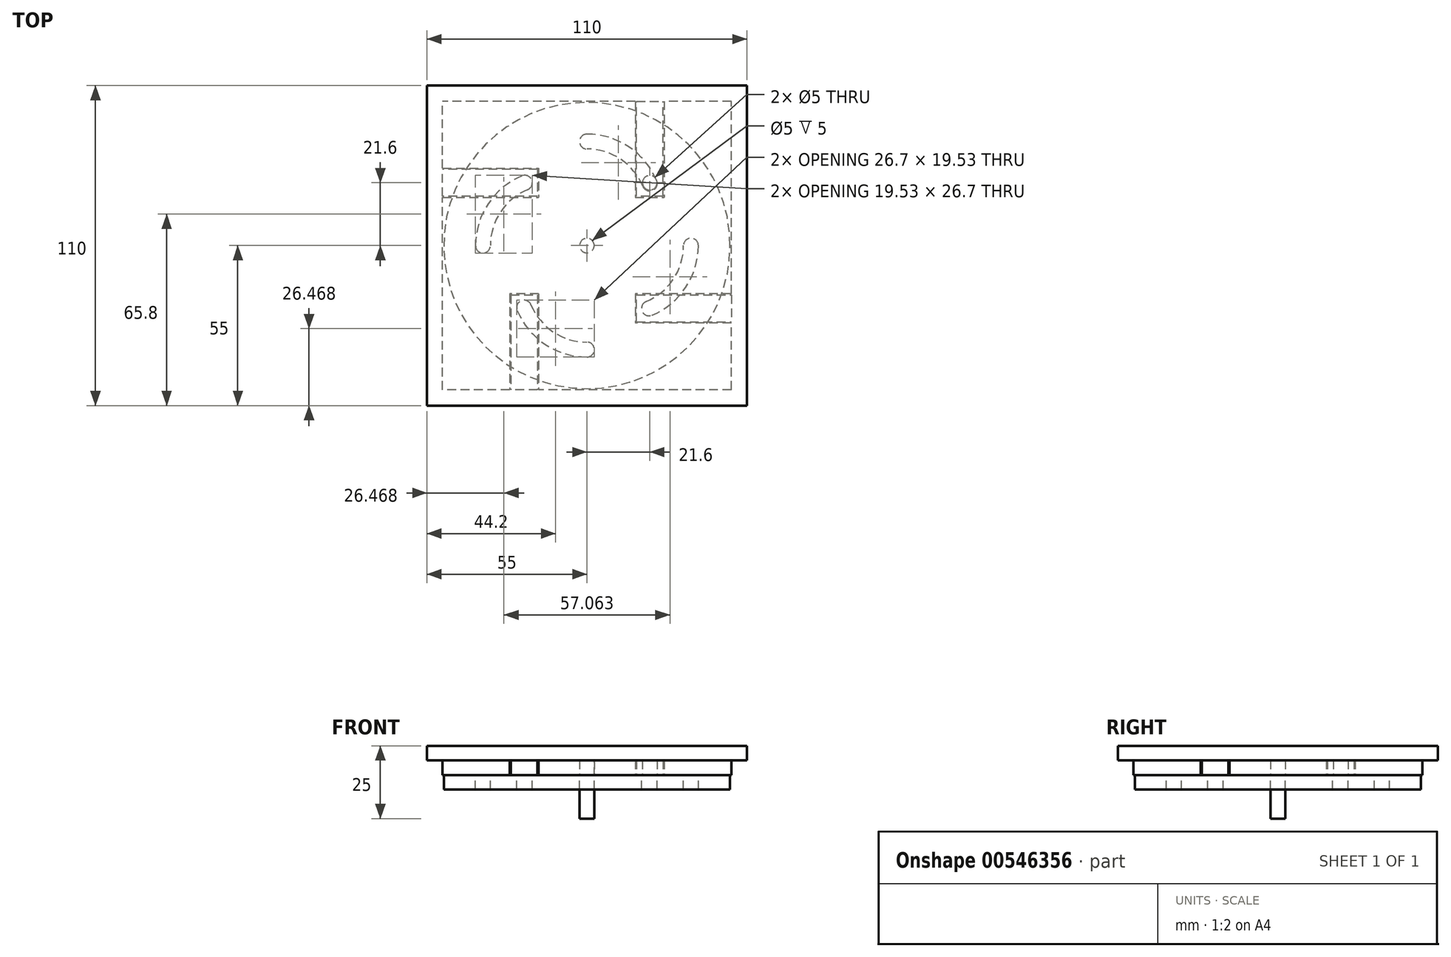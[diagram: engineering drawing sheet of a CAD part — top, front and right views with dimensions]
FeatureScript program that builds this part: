
annotation { "Feature Type Name" : "Feature", "Feature Type Description" : "" }
export const myFeature = defineFeature(function(context is Context, id is Id, definition is map)
    precondition{}
    {
        {
            assignVariable(context, id + "F0", {"name" : "thickness", "anyValue" : 5});
        }
        {
            assignVariable(context, id + "F1", {"name" : "boltsize", "anyValue" : 5});
        }
        {
            var Q0;
            Q0=qCreatedBy(makeId("Top.planeOp"),FACE);
            var sketch = newSketch(context, id + "F2", { "sketchPlane" : qUnion([Q0])});
            skPoint(sketch, "E0.middle", {"position": v(0, 0) * mm});
            skLineSegment(sketch, "E1.bottom", {"start": v(-49.6, 26.6) * mm, "end": v(-16.6, 26.6) * mm});
            skLineSegment(sketch, "E1.top", {"start": v(-49.6, 16.6) * mm, "end": v(-16.6, 16.6) * mm});
            skLineSegment(sketch, "E1.left", {"start": v(-49.6, 26.6) * mm, "end": v(-49.6, 16.6) * mm});
            skLineSegment(sketch, "E2.bottom", {"start": v(16.6, 49.6) * mm, "end": v(26.6, 49.6) * mm});
            skLineSegment(sketch, "E2.top", {"start": v(16.6, 16.6) * mm, "end": v(26.6, 16.6) * mm});
            skLineSegment(sketch, "E2.left", {"start": v(16.6, 49.6) * mm, "end": v(16.6, 16.6) * mm});
            skLineSegment(sketch, "E2.right", {"start": v(26.6, 49.6) * mm, "end": v(26.6, 16.6) * mm});
            skLineSegment(sketch, "E3.bottom", {"start": v(49.6, -16.6) * mm, "end": v(16.6, -16.6) * mm});
            skLineSegment(sketch, "E3.top", {"start": v(49.6, -26.6) * mm, "end": v(16.6, -26.6) * mm});
            skLineSegment(sketch, "E3.left", {"start": v(49.6, -16.6) * mm, "end": v(49.6, -26.6) * mm});
            skLineSegment(sketch, "E3.right", {"start": v(16.6, -16.6) * mm, "end": v(16.6, -26.6) * mm});
            skLineSegment(sketch, "E4.bottom", {"start": v(-16.6, -16.6) * mm, "end": v(-26.6, -16.6) * mm});
            skLineSegment(sketch, "E4.top", {"start": v(-16.6, -49.6) * mm, "end": v(-26.6, -49.6) * mm});
            skLineSegment(sketch, "E4.left", {"start": v(-16.6, -16.6) * mm, "end": v(-16.6, -49.6) * mm});
            skLineSegment(sketch, "E4.right", {"start": v(-26.6, -16.6) * mm, "end": v(-26.6, -49.6) * mm});
            skLineSegment(sketch, "E5.bottom", {"start": v(49.6, -49.6) * mm, "end": v(-49.6, -49.6) * mm});
            skLineSegment(sketch, "E5.top", {"start": v(49.6, 49.6) * mm, "end": v(-49.6, 49.6) * mm});
            skLineSegment(sketch, "E5.left", {"start": v(49.6, -49.6) * mm, "end": v(49.6, 49.6) * mm});
            skLineSegment(sketch, "E5.right", {"start": v(-49.6, -49.6) * mm, "end": v(-49.6, 49.6) * mm});
            skLineSegment(sketch, "E6", {"start": v(-16.6, 26.6) * mm, "end": v(-16.6, 16.6) * mm});
            skLineSegment(sketch, "E7.bottom", {"start": v(16.6, 16.6) * mm, "end": v(-16.6, 16.6) * mm, "construction": true});
            skLineSegment(sketch, "E7.top", {"start": v(16.6, -16.6) * mm, "end": v(-16.6, -16.6) * mm, "construction": true});
            skLineSegment(sketch, "E7.left", {"start": v(16.6, 16.6) * mm, "end": v(16.6, -16.6) * mm, "construction": true});
            skLineSegment(sketch, "E7.right", {"start": v(-16.6, 16.6) * mm, "end": v(-16.6, -16.6) * mm, "construction": true});
            skLineSegment(sketch, "E8.bottom", {"start": v(50, 50) * mm, "end": v(-50, 50) * mm, "construction": true});
            skLineSegment(sketch, "E8.top", {"start": v(50, -50) * mm, "end": v(-50, -50) * mm, "construction": true});
            skLineSegment(sketch, "E8.left", {"start": v(50, 50) * mm, "end": v(50, -50) * mm, "construction": true});
            skLineSegment(sketch, "E8.right", {"start": v(-50, 50) * mm, "end": v(-50, -50) * mm, "construction": true});
            skLineSegment(sketch, "E9.bottom", {"start": v(21.6, 21.6) * mm, "end": v(-21.6, 21.6) * mm, "construction": true});
            skLineSegment(sketch, "E9.top", {"start": v(21.6, -21.6) * mm, "end": v(-21.6, -21.6) * mm, "construction": true});
            skLineSegment(sketch, "E9.left", {"start": v(21.6, 21.6) * mm, "end": v(21.6, -21.6) * mm, "construction": true});
            skLineSegment(sketch, "E9.right", {"start": v(-21.6, 21.6) * mm, "end": v(-21.6, -21.6) * mm, "construction": true});
            skPoint(sketch, "E9.cornerSnap0", {"position": v(21.6, 16.6) * mm});
            skPoint(sketch, "E10", {"position": v(-16.6, 21.6) * mm});
            skLineSegment(sketch, "E11.bottom", {"start": v(26.2, 17) * mm, "end": v(17, 17) * mm});
            skLineSegment(sketch, "E11.top", {"start": v(26.2, 49.6) * mm, "end": v(17, 49.6) * mm});
            skLineSegment(sketch, "E11.left", {"start": v(26.2, 17) * mm, "end": v(26.2, 49.6) * mm});
            skLineSegment(sketch, "E11.right", {"start": v(17, 17) * mm, "end": v(17, 49.6) * mm});
            skPoint(sketch, "E11.middle", {"position": v(21.6, 33.3) * mm});
            skPoint(sketch, "E12", {"position": v(21.6, 17) * mm});
            skCircle(sketch, "E13", {"center": v(0, 0) * mm, "radius": 2.5 * mm});
            skSolve(sketch);
        }
        {
            var Q0;
            Q0=qCreatedBy(makeId("Top.planeOp"),FACE);
            var sketch = newSketch(context, id + "F3", { "sketchPlane" : qUnion([Q0])});
            skLineSegment(sketch, "E14.0", {"start": v(50, 50) * mm, "end": v(-50, 50) * mm});
            skLineSegment(sketch, "E15.0", {"start": v(-50, 50) * mm, "end": v(-50, -50) * mm});
            skLineSegment(sketch, "E16.0", {"start": v(50, 50) * mm, "end": v(50, -50) * mm});
            skLineSegment(sketch, "E17.0", {"start": v(50, -50) * mm, "end": v(-50, -50) * mm});
            skLineSegment(sketch, "E18.0", {"start": v(55, 55) * mm, "end": v(-55, 55) * mm});
            skLineSegment(sketch, "E18.1", {"start": v(55, 55) * mm, "end": v(55, -55) * mm});
            skLineSegment(sketch, "E18.2", {"start": v(55, -55) * mm, "end": v(-55, -55) * mm});
            skLineSegment(sketch, "E18.3", {"start": v(-55, 55) * mm, "end": v(-55, -55) * mm});
            skSolve(sketch);
        }
        {
            var Q0;
            {var subQ4=sQuery(id+"F2.wireOp",EDGE,"E1.bottom");Q0=makeQuery(id+"F2.imprint","IMPRINT",FACE,{"disambiguationData":[TD([[makeQuery(id+"F2.imprint","IMPRINT",EDGE,{"derivedFrom":subQ4}),1.0]])]});}
            extrude(context, id + "F4", {"entities" : qUnion([Q0]), "depth" : (getVariable(context, 'thickness')) * mm, "offsetDistance" : 25 * mm});
        }
        {
            var Q0;
            Q0=makeQuery(id+"F3.imprint","IMPRINT",FACE,{"disambiguationData":[TD([[makeQuery(id+"F3.imprint","IMPRINT",EDGE,{"derivedFrom":sQuery(id+"F3.wireOp",EDGE,"E14.0")}),-1.0]])]});
            var Q1;
            Q1=makeQuery(id+"F3.imprint","IMPRINT",FACE,{"disambiguationData":[TD([[makeQuery(id+"F3.imprint","IMPRINT",EDGE,{"derivedFrom":sQuery(id+"F3.wireOp",EDGE,"E14.0")}),1.0]])]});
            extrude(context, id + "F5", {"entities" : qUnion([Q0, Q1]), "operationType" : NewBodyOperationType.ADD, "depth" : 10 * mm, "offsetDistance" : 25 * mm, "hasSecondDirection" : true, "secondDirectionOppositeDirection" : false, "secondDirectionDepth" : 5 * mm});
        }
        {
            var Q0;
            Q0=makeQuery(id+"F2.imprint","IMPRINT",FACE,{"disambiguationData":[TD([[makeQuery(id+"F2.imprint","IMPRINT",EDGE,{"derivedFrom":sQuery(id+"F2.wireOp",EDGE,"E11.bottom")}),-1.0]])]});
            extrude(context, id + "F6", {"entities" : qUnion([Q0]), "depth" : (getVariable(context, 'thickness')) * mm, "offsetDistance" : 25 * mm});
        }
        {
            var Q0;
            Q0=qCreatedBy(makeId("Front.planeOp"),FACE);
            var sketch = newSketch(context, id + "F7", { "sketchPlane" : qUnion([Q0])});
            skLineSegment(sketch, "E19", {"start": v(0, 0) * mm, "end": v(0, 10) * mm});
            skSolve(sketch);
        }
        {
            var Q0;
            Q0=qCreatedBy(makeId("Top.planeOp"),FACE);
            var sketch = newSketch(context, id + "F8", { "sketchPlane" : qUnion([Q0])});
            skCircle(sketch, "E20", {"center": v(0, 0) * mm, "radius": 49.2 * mm});
            skSolve(sketch);
        }
        {
            var Q0;
            Q0 = qSketchRegion(id + "F8", true);
            extrude(context, id + "F9", {"entities" : qUnion([Q0]), "oppositeDirection" : true, "depth" : (getVariable(context, 'thickness')) * mm, "offsetDistance" : 25 * mm});
        }
        {
            var Q0;
            Q0=makeQuery(id+"F6.opExtrude","SWEPT_BODY",BODY,{"disambiguationData":[OSD([sQuery(id+"F2.wireOp",EDGE,"E11.bottom"),sQuery(id+"F2.wireOp",EDGE,"E11.top"),sQuery(id+"F2.wireOp",EDGE,"E11.left"),sQuery(id+"F2.wireOp",EDGE,"E11.right")])]});
            var Q1;
            Q1=sQuery(id+"F7.wireOp",EDGE,"E19");
            circularPattern(context, id + "F10", {"entities" : qUnion([Q0]), "axis" : qUnion([Q1]), "angle" : 360 * degree, "instanceCount" : 4, "equalSpace" : true});
        }
        {
            var Q0;
            Q0=sQuery(id+"F2.wireOp",VERTEX,"E9.bottom.start");
            var Q1;
            Q1=makeQuery(id+"F6.opExtrude","SWEPT_BODY",BODY,{"disambiguationData":[OSD([sQuery(id+"F2.wireOp",EDGE,"E11.bottom"),sQuery(id+"F2.wireOp",EDGE,"E11.top"),sQuery(id+"F2.wireOp",EDGE,"E11.left"),sQuery(id+"F2.wireOp",EDGE,"E11.right")])]});
            hole(context, id + "F11", {"style" : HoleStyle.SIMPLE, "endStyle" : HoleEndStyle.THROUGH, "oppositeDirection" : true, "holeDiameter" : 5 * mm, "isTappedThrough" : true, "tappedDepth" : 12 * mm, "tapClearance" : 3, "locations" : qUnion([Q0]), "scope" : qUnion([Q1])});
        }
        {
            var Q0;
            Q0=sQuery(id+"F13.wireOp",VERTEX,"E22.0");
            var Q1;
            Q1=sQuery(id+"F2.wireOp",VERTEX,"E0.middle");
            var Q2;
            Q2=makeQuery(id+"F9.opExtrude","SWEPT_BODY",BODY,{"disambiguationData":[OSD([sQuery(id+"F8.wireOp",EDGE,"E20")])]});
            hole(context, id + "F12", {"style" : HoleStyle.SIMPLE, "endStyle" : HoleEndStyle.THROUGH, "holeDiameter" : (getVariable(context, 'boltsize')) * mm, "isTappedThrough" : true, "tappedDepth" : 12 * mm, "tapClearance" : 3, "locations" : qUnion([Q0, Q1]), "scope" : qUnion([Q2])});
        }
        {
            var Q0;
            {var subQ4=sQuery(id+"F2.wireOp",EDGE,"E1.bottom");Q0=makeQuery(id+"F2.imprint","IMPRINT",FACE,{"disambiguationData":[TD([[makeQuery(id+"F2.imprint","IMPRINT",EDGE,{"derivedFrom":subQ4}),1.0]])]});}
            var sketch = newSketch(context, id + "F13", { "sketchPlane" : qUnion([Q0])});
            skCircle(sketch, "E21", {"center": v(0, 0) * mm, "radius": 30.55 * mm, "construction": true});
            skPoint(sketch, "E22.0", {"position": v(21.6, 21.6) * mm});
            skCircle(sketch, "E23", {"center": v(0, 0) * mm, "radius": 35.95 * mm, "construction": true});
            skArc(sketch, "E24", {"start": v(21.6, 21.6) * mm, "mid": v(12.97, 32.03) * mm, "end": v(0, 35.95) * mm, "construction": true});
            skPoint(sketch, "E24.second.point", {"position": v(0, 35.95) * mm});
            skPoint(sketch, "E24.third.point", {"position": v(0, 35.95) * mm});
            skArc(sketch, "E25.0.startCap", {"start": v(22.94, 22.16) * mm, "mid": v(22.16, 20.26) * mm, "end": v(20.26, 21.04) * mm});
            skArc(sketch, "E25.0.endCap", {"start": v(0, 34.5) * mm, "mid": v(-1.45, 35.95) * mm, "end": v(0, 37.4) * mm});
            skArc(sketch, "E25.0.left", {"start": v(20.26, 21.04) * mm, "mid": v(12.16, 30.83) * mm, "end": v(0, 34.5) * mm});
            skArc(sketch, "E25.0.right", {"start": v(22.94, 22.16) * mm, "mid": v(13.77, 33.24) * mm, "end": v(0, 37.4) * mm});
            skSolve(sketch);
        }
        {
            var Q0;
            Q0=qCreatedBy(makeId("Top.planeOp"),FACE);
            var sketch = newSketch(context, id + "F14", { "sketchPlane" : qUnion([Q0])});
            skCircle(sketch, "E26", {"center": v(0, 0) * mm, "radius": 30.55 * mm, "construction": true});
            skCircle(sketch, "E27", {"center": v(0, 0) * mm, "radius": 35.75 * mm, "construction": true});
            skCircle(sketch, "E28", {"center": v(0, 0) * mm, "radius": 30.35 * mm, "construction": true});
            skPoint(sketch, "E29.0", {"position": v(-21.6, 21.6) * mm});
            skPoint(sketch, "E30", {"position": v(-21.32, 21.6) * mm});
            skPoint(sketch, "E31", {"position": v(-35.75, 0) * mm});
            skArc(sketch, "E32", {"start": v(-21.8, -21.39) * mm, "mid": v(-21.56, -21.5) * mm, "end": v(-21.32, -21.6) * mm});
            skArc(sketch, "E33.trimOffspring", {"start": v(-21.32, 21.6) * mm, "mid": v(-31.8, 12.99) * mm, "end": v(-35.75, 0) * mm});
            skArc(sketch, "E34.0.startCap", {"start": v(-22.3, 23.96) * mm, "mid": v(-18.96, 22.58) * mm, "end": v(-20.34, 19.24) * mm});
            skArc(sketch, "E34.0.endCap", {"start": v(-33.2, 0) * mm, "mid": v(-35.75, -2.55) * mm, "end": v(-38.3, 0) * mm});
            skArc(sketch, "E34.0.left", {"start": v(-20.34, 19.24) * mm, "mid": v(-29.69, 11.57) * mm, "end": v(-33.2, 0) * mm});
            skArc(sketch, "E34.0.right", {"start": v(-22.3, 23.96) * mm, "mid": v(-33.93, 14.4) * mm, "end": v(-38.3, 0) * mm});
            skArc(sketch, "E35.1.0", {"start": v(-23.96, -22.3) * mm, "mid": v(-14.4, -33.93) * mm, "end": v(0, -38.3) * mm});
            skArc(sketch, "E35.1.1", {"start": v(0, -33.2) * mm, "mid": v(2.55, -35.75) * mm, "end": v(0, -38.3) * mm});
            skArc(sketch, "E35.1.2", {"start": v(-19.24, -20.34) * mm, "mid": v(-11.57, -29.69) * mm, "end": v(0, -33.2) * mm});
            skArc(sketch, "E35.1.3", {"start": v(-23.96, -22.3) * mm, "mid": v(-22.58, -18.96) * mm, "end": v(-19.24, -20.34) * mm});
            skArc(sketch, "E35.2.0", {"start": v(22.3, -23.96) * mm, "mid": v(33.93, -14.4) * mm, "end": v(38.3, 0) * mm});
            skArc(sketch, "E35.2.1", {"start": v(33.2, 0) * mm, "mid": v(35.75, 2.55) * mm, "end": v(38.3, 0) * mm});
            skArc(sketch, "E35.2.2", {"start": v(20.34, -19.24) * mm, "mid": v(29.69, -11.57) * mm, "end": v(33.2, 0) * mm});
            skArc(sketch, "E35.2.3", {"start": v(22.3, -23.96) * mm, "mid": v(18.96, -22.58) * mm, "end": v(20.34, -19.24) * mm});
            skArc(sketch, "E35.3.0", {"start": v(23.96, 22.3) * mm, "mid": v(14.4, 33.93) * mm, "end": v(0, 38.3) * mm});
            skArc(sketch, "E35.3.1", {"start": v(0, 33.2) * mm, "mid": v(-2.55, 35.75) * mm, "end": v(0, 38.3) * mm});
            skArc(sketch, "E35.3.2", {"start": v(19.24, 20.34) * mm, "mid": v(11.57, 29.69) * mm, "end": v(0, 33.2) * mm});
            skArc(sketch, "E35.3.3", {"start": v(23.96, 22.3) * mm, "mid": v(22.58, 18.96) * mm, "end": v(19.24, 20.34) * mm});
            skSolve(sketch);
        }
        {
            var Q0;
            Q0 = qSketchRegion(id + "F14", true);
            extrude(context, id + "F15", {"entities" : qUnion([Q0]), "operationType" : NewBodyOperationType.REMOVE, "endBound" : BoundingType.UP_TO_NEXT, "oppositeDirection" : true, "depth" : 25 * mm, "offsetDistance" : 25 * mm});
        }
        {
            var Q0;
            Q0=makeQuery(id+"F2.imprint","IMPRINT",FACE,{"disambiguationData":[TD([[makeQuery(id+"F2.imprint","IMPRINT",EDGE,{"derivedFrom":sQuery(id+"F2.wireOp",EDGE,"E13")}),1.0]])]});
            extrude(context, id + "F16", {"entities" : qUnion([Q0]), "oppositeDirection" : true, "depth" : (3 * getVariable(context, 'thickness')) * mm, "offsetDistance" : 25 * mm, "hasSecondDirection" : true, "secondDirectionOppositeDirection" : false, "secondDirectionDepth" : (getVariable(context, 'thickness')) * mm});
        }
    });
